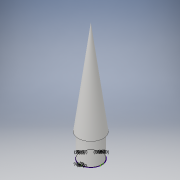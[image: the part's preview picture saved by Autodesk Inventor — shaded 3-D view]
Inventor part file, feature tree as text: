
AUTODESK INVENTOR PART (.ipt)
format: ipt  version: 2017 (Build 210142000, 142)  size: 154,624 bytes
history: native  units: in
note: dims shown in document units (in); Inventor stores cm internally (conversion verified against a paired STEP export)
features: sketch x2, revolve x1
ambient origin geometry x8: Origin, YZ Plane, XZ Plane, XY Plane, X Axis, Y Axis, Z Axis, Center Point
bodies: Solid1 (feature_tree)
feature tree (3):
  revolve  "Revolution1"  [1 undecoded]
  sketch  "Sketch2"  dims[d2=1.0in d3=0.455in d4=0.05in d5=0.05in d6=90.0deg d7=0.01in d8=0.0625in d9=0.125in d10=0.0in d11=0.0625in d12=90.0deg d13=0.0625in d14=0.0625in d15=0.0625in d20=90.0deg d21=90.0deg d23=1.5748in d25=360.0deg]
  sketch  "Sketch1"  dims[d0=4.0in d1=0.53in]
note: 1 required parameter value undecoded (feature->parameter linkage not recoverable at this tier; creation-order binding heuristic only, values carry confidence <= 0.55)
